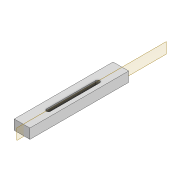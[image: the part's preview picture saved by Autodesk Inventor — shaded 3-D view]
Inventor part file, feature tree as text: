
AUTODESK INVENTOR PART (.ipt)
format: ipt  version: 2022 (Build 260153000, 153)  size: 96,256 bytes
history: native  units: mm
features: extrude x1, plane x1, sketch x1
ambient origin geometry x8: Origin, YZ Plane, XZ Plane, XY Plane, X Axis, Y Axis, Z Axis, Center Point
bodies: Solid1 (feature_tree)
feature tree (3):
  extrude  "Extrusion1"  Depth=40.0mm
  plane  "Work Plane1"
  sketch  "Sketch1"  dims[d0=3.3mm d1=40.0mm d2=10.0mm d3=10.0mm d4=20.0mm d5=20.0mm d6=6.0mm d7=8.0mm d8=0.0mm]
